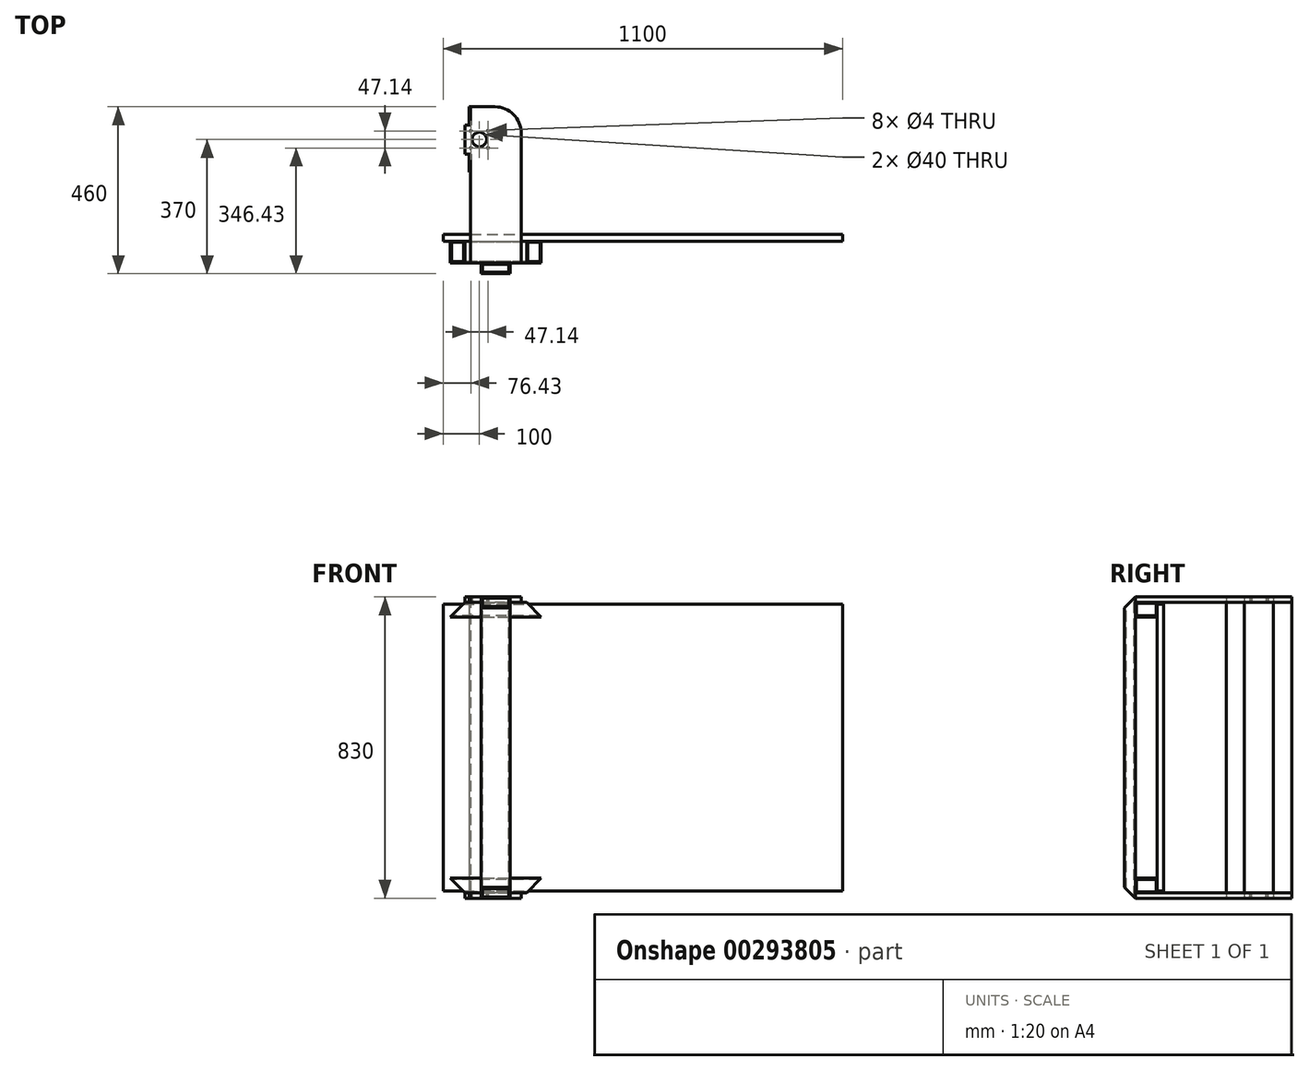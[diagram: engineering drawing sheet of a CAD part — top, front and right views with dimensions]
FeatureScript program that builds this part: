
annotation { "Feature Type Name" : "Feature", "Feature Type Description" : "" }
export const myFeature = defineFeature(function(context is Context, id is Id, definition is map)
    precondition{}
    {
        {
            var Q0;
            Q0=qCreatedBy(makeId("Top.planeOp"),FACE);
            var sketch = newSketch(context, id + "F0", { "sketchPlane" : qUnion([Q0])});
            skLineSegment(sketch, "E0", {"start": v(0, 0) * mm, "end": v(0, 300) * mm});
            skLineSegment(sketch, "E1", {"start": v(140, 357.59) * mm, "end": v(140, 0) * mm});
            skLineSegment(sketch, "E2", {"start": v(140, 0) * mm, "end": v(0, 0) * mm});
            skLineSegment(sketch, "E3", {"start": v(0, 380) * mm, "end": v(-15, 380) * mm});
            skLineSegment(sketch, "E4", {"start": v(-15, 380) * mm, "end": v(-15, 300) * mm});
            skLineSegment(sketch, "E5", {"start": v(-15, 300) * mm, "end": v(0, 300) * mm});
            skLineSegment(sketch, "E6.trimOffspring", {"start": v(0, 380) * mm, "end": v(0, 430) * mm});
            skLineSegment(sketch, "E7", {"start": v(0, 430) * mm, "end": v(67.59, 430) * mm});
            skArc(sketch, "E8", {"start": v(140, 357.59) * mm, "mid": v(118.8, 408.8) * mm, "end": v(67.59, 430) * mm});
            skPoint(sketch, "E9.middle", {"position": v(25, 340) * mm});
            skPoint(sketch, "E9.middle.positionSnap0", {"position": v(-15, 340) * mm});
            skPoint(sketch, "E9.centerSnap0", {"position": v(-15, 340) * mm});
            skLineSegment(sketch, "E10", {"start": v(-15, 340) * mm, "end": v(69.7, 340) * mm, "construction": true});
            skLineSegment(sketch, "E11", {"start": v(16, 363) * mm, "end": v(16, 308.63) * mm, "construction": true});
            skLineSegment(sketch, "E12.bottom", {"start": v(1.43, 363.57) * mm, "end": v(48.57, 363.57) * mm, "construction": true});
            skLineSegment(sketch, "E12.top", {"start": v(1.43, 316.43) * mm, "end": v(48.57, 316.43) * mm, "construction": true});
            skLineSegment(sketch, "E12.left", {"start": v(1.43, 363.57) * mm, "end": v(1.43, 316.43) * mm, "construction": true});
            skLineSegment(sketch, "E12.right", {"start": v(48.57, 363.57) * mm, "end": v(48.57, 316.43) * mm, "construction": true});
            skCircle(sketch, "E13", {"center": v(48.57, 363.57) * mm, "radius": 2 * mm});
            skCircle(sketch, "E14", {"center": v(1.43, 363.57) * mm, "radius": 2 * mm});
            skCircle(sketch, "E15", {"center": v(48.57, 316.43) * mm, "radius": 2 * mm});
            skCircle(sketch, "E16", {"center": v(1.43, 316.43) * mm, "radius": 2 * mm});
            skCircle(sketch, "E17", {"center": v(25, 340) * mm, "radius": 20 * mm});
            skSolve(sketch);
        }
        {
            var Q0;
            Q0=makeQuery(id+"F0.imprint","IMPRINT",FACE,{"disambiguationData":[TD([[makeQuery(id+"F0.imprint","IMPRINT",EDGE,{"derivedFrom":sQuery(id+"F0.wireOp",EDGE,"E0")}),-1.0]])]});
            extrude(context, id + "F1", {"entities" : qUnion([Q0]), "depth" : 15 * mm});
        }
        {
            var Q0;
            Q0=qCreatedBy(makeId("Top.planeOp"),FACE);
            var sketch = newSketch(context, id + "F2", { "sketchPlane" : qUnion([Q0])});
            skLineSegment(sketch, "E18.bottom", {"start": v(-55, 60) * mm, "end": v(195, 60) * mm});
            skLineSegment(sketch, "E18.top", {"start": v(-55, 0) * mm, "end": v(195, 0) * mm});
            skLineSegment(sketch, "E18.left", {"start": v(-55, 60) * mm, "end": v(-55, 0) * mm});
            skLineSegment(sketch, "E18.right", {"start": v(195, 60) * mm, "end": v(195, 0) * mm});
            skPoint(sketch, "E18.middle", {"position": v(70, 30) * mm});
            skSolve(sketch);
        }
        {
            var Q0;
            Q0=makeQuery(id+"F2.imprint","IMPRINT",FACE,{"disambiguationData":[TD([[makeQuery(id+"F2.imprint","IMPRINT",EDGE,{"derivedFrom":sQuery(id+"F2.wireOp",EDGE,"E18.bottom")}),-1.0]])]});
            extrude(context, id + "F3", {"entities" : qUnion([Q0]), "oppositeDirection" : true, "depth" : 40 * mm});
        }
        {
            var Q0;
            Q0=makeQuery(id+"F3.opExtrude","SWEPT_FACE",FACE,{"disambiguationData":[OSD([sQuery(id+"F2.wireOp",EDGE,"E18.left")])]});
            var sketch = newSketch(context, id + "F4", { "sketchPlane" : qUnion([Q0])});
            skLineSegment(sketch, "E19.bottom", {"start": v(-57, -3) * mm, "end": v(-3, -3) * mm});
            skLineSegment(sketch, "E19.top", {"start": v(-57, -37) * mm, "end": v(-3, -37) * mm});
            skLineSegment(sketch, "E19.left", {"start": v(-57, -3) * mm, "end": v(-57, -37) * mm});
            skLineSegment(sketch, "E19.right", {"start": v(-3, -3) * mm, "end": v(-3, -37) * mm});
            skSolve(sketch);
        }
        {
            var Q0;
            Q0=makeQuery(id+"F4.imprint","IMPRINT",FACE,{"disambiguationData":[TD([[makeQuery(id+"F4.imprint","IMPRINT",EDGE,{"derivedFrom":sQuery(id+"F4.wireOp",EDGE,"E19.bottom")}),-1.0]])]});
            extrude(context, id + "F5", {"entities" : qUnion([Q0]), "operationType" : NewBodyOperationType.REMOVE, "endBound" : BoundingType.UP_TO_NEXT, "oppositeDirection" : true, "depth" : 25 * mm});
        }
        {
            var Q0;
            Q0=makeQuery(id+"F3.opExtrude","SWEPT_FACE",FACE,{"disambiguationData":[OSD([sQuery(id+"F2.wireOp",EDGE,"E18.bottom")])]});
            var sketch = newSketch(context, id + "F6", { "sketchPlane" : qUnion([Q0])});
            skLineSegment(sketch, "E20", {"start": v(-195, -40) * mm, "end": v(-195, 0) * mm});
            skLineSegment(sketch, "E21", {"start": v(-195, 0) * mm, "end": v(-155, 0) * mm});
            skLineSegment(sketch, "E22", {"start": v(-155, 0) * mm, "end": v(-195, -40) * mm});
            skLineSegment(sketch, "E23", {"start": v(15, 0) * mm, "end": v(55, 0) * mm});
            skLineSegment(sketch, "E24", {"start": v(55, 0) * mm, "end": v(55, -40) * mm});
            skLineSegment(sketch, "E25", {"start": v(55, -40) * mm, "end": v(15, 0) * mm});
            skSolve(sketch);
        }
        {
            var Q0;
            Q0=makeQuery(id+"F6.imprint","IMPRINT",FACE,{"disambiguationData":[TD([[makeQuery(id+"F6.imprint","IMPRINT",EDGE,{"derivedFrom":sQuery(id+"F6.wireOp",EDGE,"E20")}),-1.0]])]});
            var Q1;
            Q1=makeQuery(id+"F6.imprint","IMPRINT",FACE,{"disambiguationData":[TD([[makeQuery(id+"F6.imprint","IMPRINT",EDGE,{"derivedFrom":sQuery(id+"F6.wireOp",EDGE,"E23")}),1.0]])]});
            extrude(context, id + "F7", {"entities" : qUnion([Q0, Q1]), "operationType" : NewBodyOperationType.REMOVE, "oppositeDirection" : true, "depth" : 60 * mm});
        }
        {
            var Q0;
            Q0=qCreatedBy(makeId("Front.planeOp"),FACE);
            var sketch = newSketch(context, id + "F8", { "sketchPlane" : qUnion([Q0])});
            skLineSegment(sketch, "E26.bottom", {"start": v(30, 15) * mm, "end": v(110, 15) * mm});
            skLineSegment(sketch, "E26.top", {"start": v(30, -815) * mm, "end": v(110, -815) * mm});
            skLineSegment(sketch, "E26.left", {"start": v(30, 15) * mm, "end": v(30, -815) * mm});
            skLineSegment(sketch, "E26.right", {"start": v(110, 15) * mm, "end": v(110, -815) * mm});
            skLineSegment(sketch, "E27", {"start": v(30, -400) * mm, "end": v(110, -400) * mm, "construction": true});
            skSolve(sketch);
        }
        {
            var Q0;
            Q0=makeQuery(id+"F8.imprint","IMPRINT",FACE,{"disambiguationData":[TD([[makeQuery(id+"F8.imprint","IMPRINT",EDGE,{"derivedFrom":sQuery(id+"F8.wireOp",EDGE,"E26.bottom")}),-1.0]])]});
            extrude(context, id + "F9", {"entities" : qUnion([Q0]), "depth" : 30 * mm});
        }
        {
            var Q0;
            Q0=makeQuery(id+"F9.opExtrude","SWEPT_FACE",FACE,{"disambiguationData":[OSD([sQuery(id+"F8.wireOp",EDGE,"E26.bottom")])]});
            var sketch = newSketch(context, id + "F10", { "sketchPlane" : qUnion([Q0])});
            skLineSegment(sketch, "E28.bottom", {"start": v(106, -4) * mm, "end": v(34, -4) * mm});
            skLineSegment(sketch, "E28.top", {"start": v(106, -26) * mm, "end": v(34, -26) * mm});
            skLineSegment(sketch, "E28.left", {"start": v(106, -4) * mm, "end": v(106, -26) * mm});
            skLineSegment(sketch, "E28.right", {"start": v(34, -4) * mm, "end": v(34, -26) * mm});
            skSolve(sketch);
        }
        {
            var Q0;
            Q0=makeQuery(id+"F10.imprint","IMPRINT",FACE,{"disambiguationData":[TD([[makeQuery(id+"F10.imprint","IMPRINT",EDGE,{"derivedFrom":sQuery(id+"F10.wireOp",EDGE,"E28.bottom")}),1.0]])]});
            extrude(context, id + "F11", {"entities" : qUnion([Q0]), "operationType" : NewBodyOperationType.REMOVE, "endBound" : BoundingType.UP_TO_NEXT, "oppositeDirection" : true, "depth" : 25 * mm});
        }
        {
            var Q0;
            Q0=makeQuery(id+"F9.opExtrude","SWEPT_FACE",FACE,{"disambiguationData":[OSD([sQuery(id+"F8.wireOp",EDGE,"E26.right")])]});
            var sketch = newSketch(context, id + "F12", { "sketchPlane" : qUnion([Q0])});
            skLineSegment(sketch, "E29", {"start": v(-30, -15) * mm, "end": v(-30, 15) * mm});
            skLineSegment(sketch, "E30", {"start": v(-30, 15) * mm, "end": v(0, 15) * mm});
            skLineSegment(sketch, "E31", {"start": v(0, 15) * mm, "end": v(-30, -15) * mm});
            skLineSegment(sketch, "E32", {"start": v(-30, -815) * mm, "end": v(-30, -785) * mm});
            skLineSegment(sketch, "E33", {"start": v(-30, -785) * mm, "end": v(0, -815) * mm});
            skLineSegment(sketch, "E34", {"start": v(0, -815) * mm, "end": v(-30, -815) * mm});
            skSolve(sketch);
        }
        {
            var Q0;
            Q0=makeQuery(id+"F12.imprint","IMPRINT",FACE,{"disambiguationData":[TD([[makeQuery(id+"F12.imprint","IMPRINT",EDGE,{"derivedFrom":sQuery(id+"F12.wireOp",EDGE,"E29")}),1.0]])]});
            var Q1;
            Q1=makeQuery(id+"F12.imprint","IMPRINT",FACE,{"disambiguationData":[TD([[makeQuery(id+"F12.imprint","IMPRINT",EDGE,{"derivedFrom":sQuery(id+"F12.wireOp",EDGE,"E32")}),1.0]])]});
            extrude(context, id + "F13", {"entities" : qUnion([Q0, Q1]), "operationType" : NewBodyOperationType.REMOVE, "oppositeDirection" : true, "depth" : 80 * mm});
        }
        {
            var Q0;
            Q0=qCreatedBy(makeId("Top.planeOp"),FACE);
            cPlane(context, id + "F14", {"entities" : qUnion([Q0]), "cplaneType" : CPlaneType.OFFSET, "offset" : 400 * mm, "oppositeDirection" : true, "width" : 150 * mm, "height" : 150 * mm});
        }
        {
            var Q0;
            Q0=makeQuery(id+"F3.opExtrude","SWEPT_BODY",BODY,{"disambiguationData":[OSD([sQuery(id+"F2.wireOp",EDGE,"E18.bottom"),sQuery(id+"F2.wireOp",EDGE,"E18.top"),sQuery(id+"F2.wireOp",EDGE,"E18.left"),sQuery(id+"F2.wireOp",EDGE,"E18.right")])]});
            var Q1;
            Q1=makeQuery(id+"F1.opExtrude","SWEPT_BODY",BODY,{"disambiguationData":[OSD([sQuery(id+"F0.wireOp",EDGE,"E0"),sQuery(id+"F0.wireOp",EDGE,"E1"),sQuery(id+"F0.wireOp",EDGE,"E2"),sQuery(id+"F0.wireOp",EDGE,"E3"),sQuery(id+"F0.wireOp",EDGE,"E4"),sQuery(id+"F0.wireOp",EDGE,"E5"),sQuery(id+"F0.wireOp",EDGE,"E6.trimOffspring"),sQuery(id+"F0.wireOp",EDGE,"E7"),sQuery(id+"F0.wireOp",EDGE,"E8")])]});
            var Q2;
            Q2=qCreatedBy(id+"F14.planeOp",FACE);
            mirror(context, id + "F15", {"entities" : qUnion([Q0, Q1]), "mirrorPlane" : qUnion([Q2])});
        }
        {
            var Q0;
            Q0=makeQuery(id+"F1.opExtrude","SWEPT_FACE",FACE,{"disambiguationData":[OSD([sQuery(id+"F0.wireOp",EDGE,"E6.trimOffspring")])]});
            var sketch = newSketch(context, id + "F16", { "sketchPlane" : qUnion([Q0])});
            skLineSegment(sketch, "E35.bottom", {"start": v(-430, 15) * mm, "end": v(-380, 15) * mm});
            skLineSegment(sketch, "E35.top", {"start": v(-430, -815) * mm, "end": v(-380, -815) * mm});
            skLineSegment(sketch, "E35.left", {"start": v(-430, 15) * mm, "end": v(-430, -815) * mm});
            skLineSegment(sketch, "E35.right", {"start": v(-380, 15) * mm, "end": v(-380, -815) * mm});
            skLineSegment(sketch, "E36.bottom", {"start": v(-250, 15) * mm, "end": v(-300, 15) * mm});
            skLineSegment(sketch, "E36.top", {"start": v(-250, -815) * mm, "end": v(-300, -815) * mm});
            skLineSegment(sketch, "E36.left", {"start": v(-250, 15) * mm, "end": v(-250, -815) * mm});
            skLineSegment(sketch, "E36.right", {"start": v(-300, 15) * mm, "end": v(-300, -815) * mm});
            skSolve(sketch);
        }
        {
            var Q0;
            Q0 = qSketchRegion(id + "F16", true);
            extrude(context, id + "F17", {"entities" : qUnion([Q0]), "depth" : 3 * mm});
        }
        {
            var Q0;
            Q0=qCreatedBy(makeId("Front.planeOp"),FACE);
            cPlane(context, id + "F18", {"entities" : qUnion([Q0]), "cplaneType" : CPlaneType.OFFSET, "offset" : 60 * mm, "oppositeDirection" : true, "width" : 150 * mm, "height" : 150 * mm});
        }
        {
            var Q0;
            Q0=qCreatedBy(id+"F18.planeOp",FACE);
            var sketch = newSketch(context, id + "F19", { "sketchPlane" : qUnion([Q0])});
            skLineSegment(sketch, "E37.bottom", {"start": v(-75, -5) * mm, "end": v(1025, -5) * mm});
            skLineSegment(sketch, "E37.top", {"start": v(-75, -795) * mm, "end": v(1025, -795) * mm});
            skLineSegment(sketch, "E37.left", {"start": v(-75, -5) * mm, "end": v(-75, -795) * mm});
            skLineSegment(sketch, "E37.right", {"start": v(1025, -5) * mm, "end": v(1025, -795) * mm});
            skSolve(sketch);
        }
        {
            var Q0;
            Q0=makeQuery(id+"F19.imprint","IMPRINT",FACE,{"disambiguationData":[TD([[makeQuery(id+"F19.imprint","IMPRINT",EDGE,{"derivedFrom":sQuery(id+"F19.wireOp",EDGE,"E37.bottom")}),-1.0]])]});
            extrude(context, id + "F20", {"entities" : qUnion([Q0]), "oppositeDirection" : true, "depth" : 18 * mm});
        }
    });
